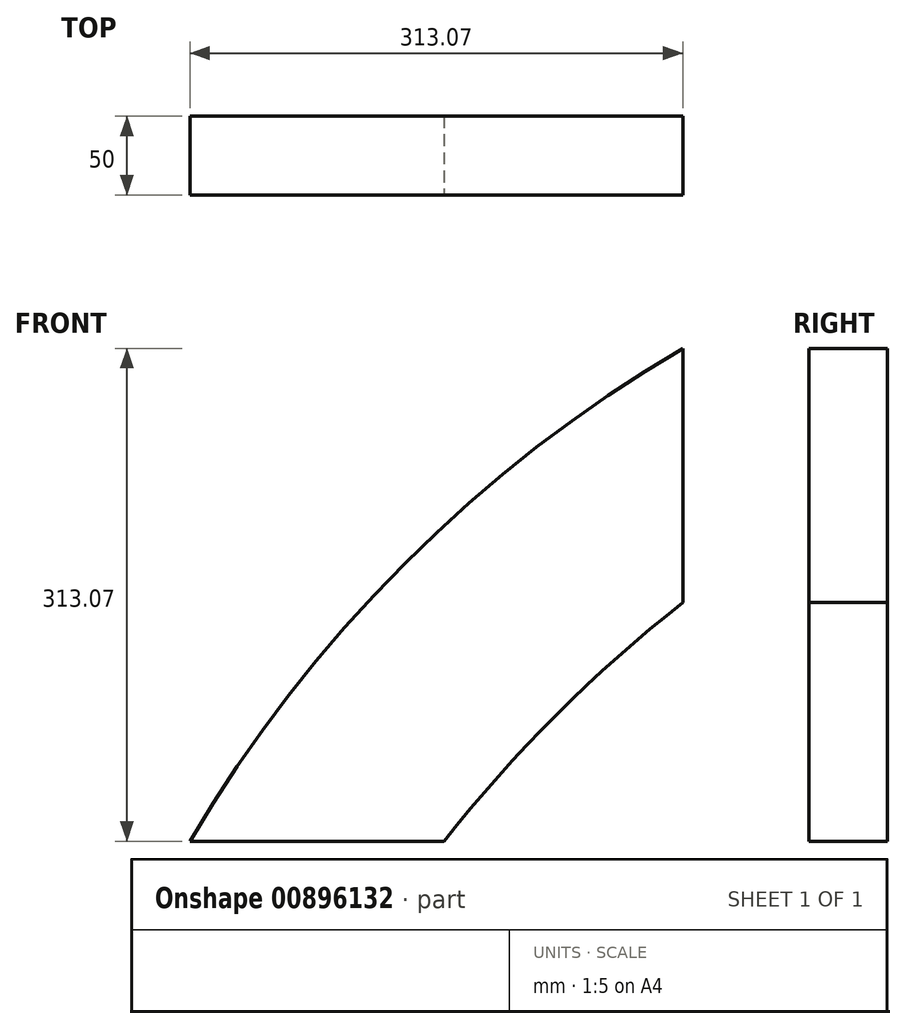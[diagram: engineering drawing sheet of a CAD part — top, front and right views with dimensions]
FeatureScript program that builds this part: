
annotation { "Feature Type Name" : "Feature", "Feature Type Description" : "" }
export const myFeature = defineFeature(function(context is Context, id is Id, definition is map)
    precondition{}
    {
        {
            var Q0;
            Q0=qCreatedBy(makeId("Front.planeOp"),FACE);
            var sketch = newSketch(context, id + "F0", { "sketchPlane" : qUnion([Q0])});
            skLineSegment(sketch, "E0.bottom", {"start": v(0, 0) * mm, "end": v(500, 0) * mm});
            skLineSegment(sketch, "E0.top", {"start": v(0, 500) * mm, "end": v(500, 500) * mm});
            skLineSegment(sketch, "E0.left", {"start": v(0, 0) * mm, "end": v(0, 500) * mm});
            skLineSegment(sketch, "E0.right", {"start": v(500, 0) * mm, "end": v(500, 500) * mm});
            skLineSegment(sketch, "E1", {"start": v(500, 500) * mm, "end": v(0, 0) * mm});
            skLineSegment(sketch, "E2", {"start": v(0, 500) * mm, "end": v(500, 0) * mm});
            skLineSegment(sketch, "E3", {"start": v(0, 500) * mm, "end": v(1101.65, -601.65) * mm});
            skCircle(sketch, "E4", {"center": v(945.51, -445.51) * mm, "radius": 879.74 * mm});
            skCircle(sketch, "E5", {"center": v(1056.9, -556.9) * mm, "radius": 901.22 * mm});
            skSolve(sketch);
        }
        {
            var Q0;
            {var subQ0=sQuery(id+"F0.wireOp",EDGE,"E4");var subQ1=sQuery(id+"F0.wireOp",EDGE,"E0.bottom");var subQ2=makeQuery(id+"F0.imprint","INTERSECT",VERTEX,{"derivedFrom":[subQ1,subQ0]});Q0=makeQuery(id+"F0.imprint","IMPRINT",FACE,{"disambiguationData":[TD([[makeQuery(id+"F0.imprint","IMPRINT",EDGE,{"disambiguationData":[TD([[subQ2,-1.0]])],"derivedFrom":subQ1}),1.0]])]});}
            var Q1;
            {var subQ0=sQuery(id+"F0.wireOp",EDGE,"E4");var subQ1=sQuery(id+"F0.wireOp",EDGE,"E0.right");var subQ2=makeQuery(id+"F0.imprint","INTERSECT",VERTEX,{"derivedFrom":[subQ1,subQ0]});Q1=makeQuery(id+"F0.imprint","IMPRINT",FACE,{"disambiguationData":[TD([[makeQuery(id+"F0.imprint","IMPRINT",EDGE,{"disambiguationData":[TD([[subQ2,1.0]])],"derivedFrom":subQ1}),1.0]])]});}
            extrude(context, id + "F1", {"entities" : qUnion([Q0, Q1]), "oppositeDirection" : true, "depth" : 50 * mm, "offsetDistance" : 25 * mm});
        }
    });
